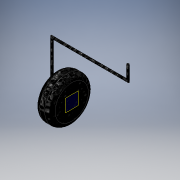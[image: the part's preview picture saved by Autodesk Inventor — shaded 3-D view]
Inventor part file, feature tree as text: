
AUTODESK INVENTOR PART (.ipt)
format: ipt  version: 2018 (Build 220112000, 112)  size: 138,240 bytes
history: native  units: in
note: dims shown in document units (in); Inventor stores cm internally (conversion verified against a paired STEP export)
features: sketch x3, plane x1, extrude x1, fillet x1, sweep x1
ambient origin geometry x8: Origin, YZ Plane, XZ Plane, XY Plane, X Axis, Y Axis, Z Axis, Center Point
bodies: Solid1 (feature_tree)
feature tree (7):
  sketch  "3D Sketch1"
  plane  "Work Plane1"
  extrude  "Extrusion1"  Depth=3.1496in
  fillet  "Fillet1"  Radius=5.1575in
  sweep  "Sweep1"
  sketch  "Sketch1"  dims[d0=1.3386in d1=3.1496in d2=5.1575in]
  sketch  "Sketch2"  dims[d3=0.9843in d4=2.9724in d5=1.0433in d6=0.0in d7=0.3543in d8=0.1575in d9=0.0in d10=0.0in]
